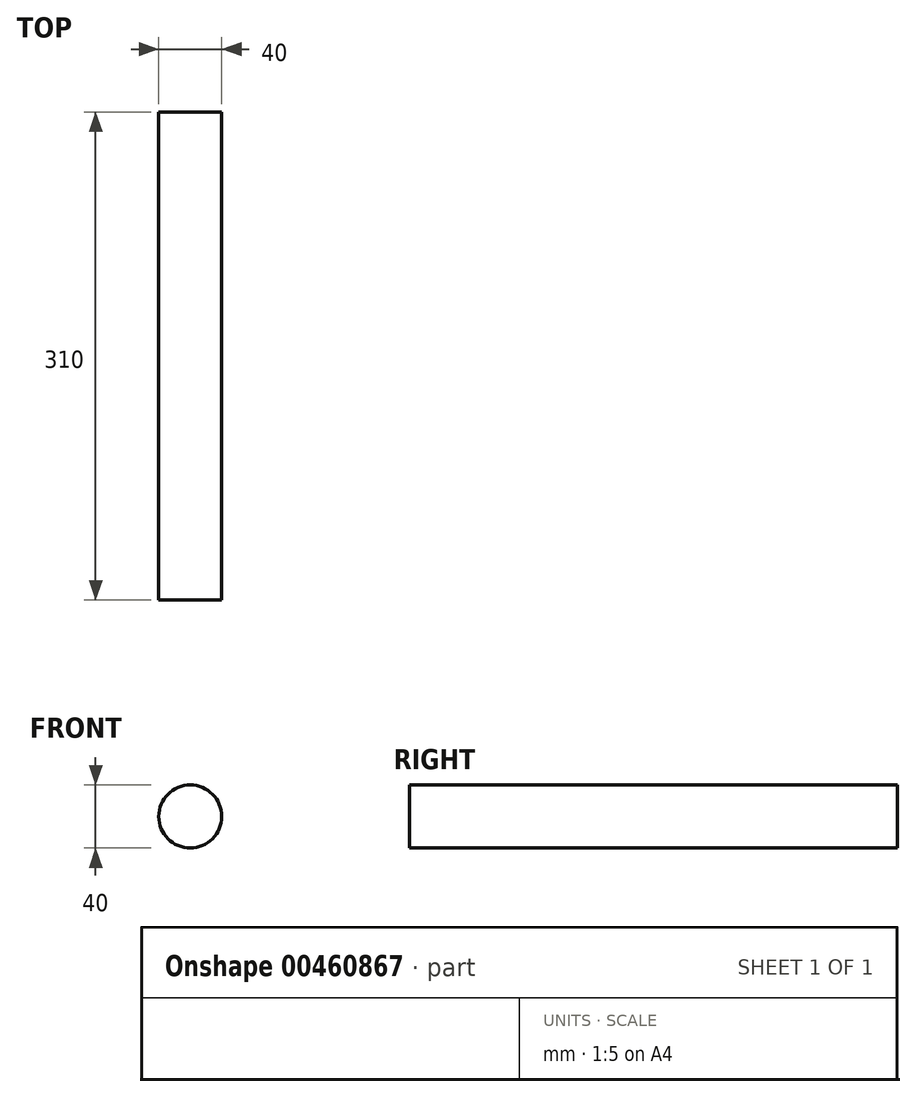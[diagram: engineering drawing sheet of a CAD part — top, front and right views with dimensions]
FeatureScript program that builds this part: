
annotation { "Feature Type Name" : "Feature", "Feature Type Description" : "" }
export const myFeature = defineFeature(function(context is Context, id is Id, definition is map)
    precondition{}
    {
        {
            var Q0;
            Q0=qCreatedBy(makeId("Front.planeOp"),FACE);
            var sketch = newSketch(context, id + "F0", { "sketchPlane" : qUnion([Q0])});
            skCircle(sketch, "E0", {"center": v(21.34, 16.24) * mm, "radius": 20 * mm});
            skSolve(sketch);
        }
        {
            var Q0;
            Q0=makeQuery(id+"F0.imprint","IMPRINT",FACE,{"disambiguationData":[TD([[makeQuery(id+"F0.imprint","IMPRINT",EDGE,{"derivedFrom":sQuery(id+"F0.wireOp",EDGE,"E0")}),1.0]])]});
            extrude(context, id + "F1", {"entities" : qUnion([Q0]), "depth" : 310 * mm});
        }
    });
